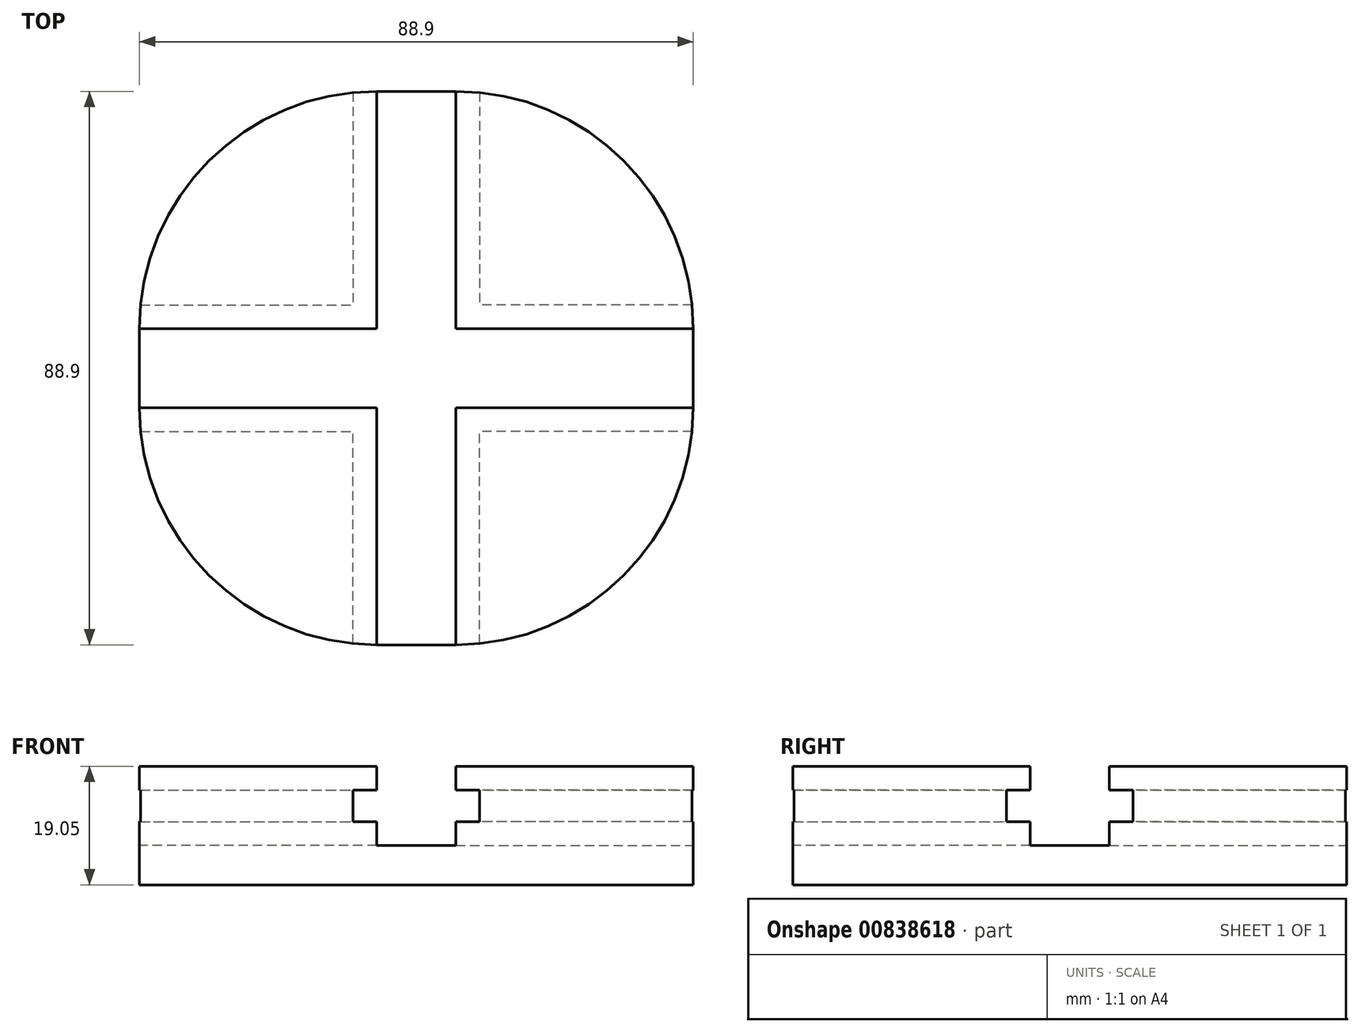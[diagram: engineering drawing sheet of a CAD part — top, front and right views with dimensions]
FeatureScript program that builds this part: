
annotation { "Feature Type Name" : "Feature", "Feature Type Description" : "" }
export const myFeature = defineFeature(function(context is Context, id is Id, definition is map)
    precondition{}
    {
        {
            var Q0;
            Q0=qCreatedBy(makeId("Top.planeOp"),FACE);
            var sketch = newSketch(context, id + "F0", { "sketchPlane" : qUnion([Q0])});
            skLineSegment(sketch, "E0.bottom", {"start": v(0, 0) * mm, "end": v(88.9, 0) * mm});
            skLineSegment(sketch, "E0.top", {"start": v(0, 88.9) * mm, "end": v(88.9, 88.9) * mm});
            skLineSegment(sketch, "E0.left", {"start": v(0, 0) * mm, "end": v(0, 88.9) * mm});
            skLineSegment(sketch, "E0.right", {"start": v(88.9, 0) * mm, "end": v(88.9, 88.9) * mm});
            skSolve(sketch);
        }
        {
            var Q0;
            Q0=makeQuery(id+"F0.imprint","IMPRINT",FACE,{"disambiguationData":[TD([[makeQuery(id+"F0.imprint","IMPRINT",EDGE,{"derivedFrom":sQuery(id+"F0.wireOp",EDGE,"E0.bottom")}),1.0]])]});
            extrude(context, id + "F1", {"entities" : qUnion([Q0]), "depth" : 19.05 * mm, "offsetDistance" : 25.4 * mm});
        }
        {
            var Q0;
            Q0=makeQuery(id+"F1.opExtrude","CAP_FACE",FACE,{"disambiguationData":[OSD([sQuery(id+"F0.wireOp",EDGE,"E0.bottom"),sQuery(id+"F0.wireOp",EDGE,"E0.top"),sQuery(id+"F0.wireOp",EDGE,"E0.left"),sQuery(id+"F0.wireOp",EDGE,"E0.right")])],"isStart":false});
            var sketch = newSketch(context, id + "F2", { "sketchPlane" : qUnion([Q0])});
            skLineSegment(sketch, "E1", {"start": v(0, 50.8) * mm, "end": v(38.1, 50.8) * mm});
            skLineSegment(sketch, "E2", {"start": v(38.1, 50.8) * mm, "end": v(38.1, 88.9) * mm});
            skLineSegment(sketch, "E3", {"start": v(38.1, 88.9) * mm, "end": v(50.8, 88.9) * mm});
            skLineSegment(sketch, "E4", {"start": v(50.8, 88.9) * mm, "end": v(50.8, 50.8) * mm});
            skLineSegment(sketch, "E5", {"start": v(50.8, 50.8) * mm, "end": v(88.9, 50.8) * mm});
            skLineSegment(sketch, "E6", {"start": v(88.9, 50.8) * mm, "end": v(88.9, 38.1) * mm});
            skLineSegment(sketch, "E7", {"start": v(88.9, 38.1) * mm, "end": v(50.8, 38.1) * mm});
            skLineSegment(sketch, "E8", {"start": v(50.8, 38.1) * mm, "end": v(50.8, 0) * mm});
            skLineSegment(sketch, "E9", {"start": v(50.8, 0) * mm, "end": v(38.1, 0) * mm});
            skLineSegment(sketch, "E10", {"start": v(38.1, 0) * mm, "end": v(38.1, 38.1) * mm});
            skLineSegment(sketch, "E11", {"start": v(38.1, 38.1) * mm, "end": v(0, 38.1) * mm});
            skSolve(sketch);
        }
        {
            var Q0;
            {var subQ0=sQuery(id+"F2.wireOp",EDGE,"E1");Q0=makeQuery(id+"F2.imprint","IMPRINT",FACE,{"disambiguationData":[TD([[makeQuery(id+"F2.imprint","IMPRINT",EDGE,{"derivedFrom":subQ0}),-1.0]])]});}
            extrude(context, id + "F3", {"entities" : qUnion([Q0]), "operationType" : NewBodyOperationType.REMOVE, "oppositeDirection" : true, "depth" : 12.7 * mm, "offsetDistance" : 25.4 * mm});
        }
        {
            var Q0;
            Q0=makeQuery(id+"F1.opExtrude","SWEPT_EDGE",EDGE,{"disambiguationData":[OSD([sQuery(id+"F0.wireOp",EDGE,"E0.bottom"),sQuery(id+"F0.wireOp",EDGE,"E0.right")])]});
            var Q1;
            Q1=makeQuery(id+"F1.opExtrude","SWEPT_EDGE",EDGE,{"disambiguationData":[OSD([sQuery(id+"F0.wireOp",EDGE,"E0.bottom"),sQuery(id+"F0.wireOp",EDGE,"E0.left")])]});
            var Q2;
            Q2=makeQuery(id+"F1.opExtrude","SWEPT_EDGE",EDGE,{"disambiguationData":[OSD([sQuery(id+"F0.wireOp",EDGE,"E0.top"),sQuery(id+"F0.wireOp",EDGE,"E0.right")])]});
            var Q3;
            Q3=makeQuery(id+"F1.opExtrude","SWEPT_EDGE",EDGE,{"disambiguationData":[OSD([sQuery(id+"F0.wireOp",EDGE,"E0.top"),sQuery(id+"F0.wireOp",EDGE,"E0.left")])]});
            fillet(context, id + "F4", {"entities" : qUnion([Q0, Q1, Q2, Q3]), "radius" : 38.1 * mm, "tangentPropagation" : true, "allowEdgeOverflow" : false});
        }
        {
            var Q0;
            Q0=makeQuery(id+"F3.boolean.opBoolean","COPY",FACE,{"derivedFrom":makeQuery(id+"F3.opExtrude","SWEPT_FACE",FACE,{"disambiguationData":[OSD([sQuery(id+"F2.wireOp",EDGE,"E7")])]})});
            var sketch = newSketch(context, id + "F5", { "sketchPlane" : qUnion([Q0])});
            skLineSegment(sketch, "E12", {"start": v(-50.8, 15.24) * mm, "end": v(-54.61, 15.24) * mm});
            skLineSegment(sketch, "E13", {"start": v(-54.61, 15.24) * mm, "end": v(-54.61, 10.16) * mm});
            skLineSegment(sketch, "E14", {"start": v(-54.61, 10.16) * mm, "end": v(-50.8, 10.16) * mm});
            skLineSegment(sketch, "E15", {"start": v(-50.8, 10.16) * mm, "end": v(-50.8, 15.24) * mm});
            skSolve(sketch);
        }
        {
            var Q0;
            Q0=makeQuery(id+"F5.imprint","IMPRINT",FACE,{"disambiguationData":[TD([[makeQuery(id+"F5.imprint","IMPRINT",EDGE,{"derivedFrom":sQuery(id+"F5.wireOp",EDGE,"E12")}),1.0]])]});
            extrude(context, id + "F6", {"entities" : qUnion([Q0]), "operationType" : NewBodyOperationType.REMOVE, "oppositeDirection" : true, "depth" : 38.1 * mm, "offsetDistance" : 25.4 * mm});
        }
        {
            var Q0;
            Q0=makeQuery(id+"F3.boolean.opBoolean","COPY",FACE,{"derivedFrom":makeQuery(id+"F3.opExtrude","SWEPT_FACE",FACE,{"disambiguationData":[OSD([sQuery(id+"F2.wireOp",EDGE,"E5")])]})});
            var sketch = newSketch(context, id + "F7", { "sketchPlane" : qUnion([Q0])});
            skLineSegment(sketch, "E16", {"start": v(50.8, 15.24) * mm, "end": v(54.61, 15.24) * mm});
            skLineSegment(sketch, "E17", {"start": v(54.61, 15.24) * mm, "end": v(54.61, 10.16) * mm});
            skLineSegment(sketch, "E18", {"start": v(54.61, 10.16) * mm, "end": v(50.8, 10.16) * mm});
            skLineSegment(sketch, "E19", {"start": v(50.8, 10.16) * mm, "end": v(50.8, 15.24) * mm});
            skSolve(sketch);
        }
        {
            var Q0;
            Q0=makeQuery(id+"F7.imprint","IMPRINT",FACE,{"disambiguationData":[TD([[makeQuery(id+"F7.imprint","IMPRINT",EDGE,{"derivedFrom":sQuery(id+"F7.wireOp",EDGE,"E16")}),-1.0]])]});
            extrude(context, id + "F8", {"entities" : qUnion([Q0]), "operationType" : NewBodyOperationType.REMOVE, "oppositeDirection" : true, "depth" : 38.1 * mm, "offsetDistance" : 25.4 * mm});
        }
        {
            var Q0;
            Q0=makeQuery(id+"F3.boolean.opBoolean","COPY",FACE,{"derivedFrom":makeQuery(id+"F3.opExtrude","SWEPT_FACE",FACE,{"disambiguationData":[OSD([sQuery(id+"F2.wireOp",EDGE,"E10")])]})});
            var sketch = newSketch(context, id + "F9", { "sketchPlane" : qUnion([Q0])});
            skLineSegment(sketch, "E20.bottom", {"start": v(38.1, 15.24) * mm, "end": v(34.3, 15.24) * mm});
            skLineSegment(sketch, "E20.top", {"start": v(38.1, 10.16) * mm, "end": v(34.3, 10.16) * mm});
            skLineSegment(sketch, "E20.left", {"start": v(38.1, 15.24) * mm, "end": v(38.1, 10.16) * mm});
            skLineSegment(sketch, "E20.right", {"start": v(34.3, 15.24) * mm, "end": v(34.3, 10.16) * mm});
            skSolve(sketch);
        }
        {
            var Q0;
            Q0=makeQuery(id+"F9.imprint","IMPRINT",FACE,{"disambiguationData":[TD([[makeQuery(id+"F9.imprint","IMPRINT",EDGE,{"derivedFrom":sQuery(id+"F9.wireOp",EDGE,"E20.bottom")}),1.0]])]});
            extrude(context, id + "F10", {"entities" : qUnion([Q0]), "operationType" : NewBodyOperationType.REMOVE, "oppositeDirection" : true, "depth" : 38.1 * mm, "offsetDistance" : 25.4 * mm});
        }
        {
            var Q0;
            Q0=makeQuery(id+"F6.boolean.opBoolean","COPY",FACE,{"derivedFrom":makeQuery(id+"F6.opExtrude","SWEPT_FACE",FACE,{"disambiguationData":[OSD([sQuery(id+"F5.wireOp",EDGE,"E13")])]})});
            var sketch = newSketch(context, id + "F11", { "sketchPlane" : qUnion([Q0])});
            skLineSegment(sketch, "E21", {"start": v(-38.1, 15.24) * mm, "end": v(-34.3, 15.24) * mm});
            skLineSegment(sketch, "E22", {"start": v(-34.3, 15.24) * mm, "end": v(-34.3, 10.16) * mm});
            skLineSegment(sketch, "E23", {"start": v(-34.3, 10.16) * mm, "end": v(-38.1, 10.16) * mm});
            skLineSegment(sketch, "E24", {"start": v(-38.1, 10.16) * mm, "end": v(-38.1, 15.24) * mm});
            skSolve(sketch);
        }
        {
            var Q0;
            Q0=makeQuery(id+"F11.imprint","IMPRINT",FACE,{"disambiguationData":[TD([[makeQuery(id+"F11.imprint","IMPRINT",EDGE,{"derivedFrom":sQuery(id+"F11.wireOp",EDGE,"E21")}),1.0]])]});
            extrude(context, id + "F12", {"entities" : qUnion([Q0]), "operationType" : NewBodyOperationType.REMOVE, "oppositeDirection" : true, "depth" : 38.1 * mm, "offsetDistance" : 25.4 * mm});
        }
        {
            var Q0;
            Q0=makeQuery(id+"F3.boolean.opBoolean","COPY",FACE,{"derivedFrom":makeQuery(id+"F3.opExtrude","SWEPT_FACE",FACE,{"disambiguationData":[OSD([sQuery(id+"F2.wireOp",EDGE,"E2")])]})});
            var sketch = newSketch(context, id + "F13", { "sketchPlane" : qUnion([Q0])});
            skLineSegment(sketch, "E25.bottom", {"start": v(50.8, 15.24) * mm, "end": v(54.6, 15.24) * mm});
            skLineSegment(sketch, "E25.top", {"start": v(50.8, 10.16) * mm, "end": v(54.6, 10.16) * mm});
            skLineSegment(sketch, "E25.left", {"start": v(50.8, 15.24) * mm, "end": v(50.8, 10.16) * mm});
            skLineSegment(sketch, "E25.right", {"start": v(54.6, 15.24) * mm, "end": v(54.6, 10.16) * mm});
            skSolve(sketch);
        }
        {
            var Q0;
            Q0=makeQuery(id+"F13.imprint","IMPRINT",FACE,{"disambiguationData":[TD([[makeQuery(id+"F13.imprint","IMPRINT",EDGE,{"derivedFrom":sQuery(id+"F13.wireOp",EDGE,"E25.bottom")}),-1.0]])]});
            extrude(context, id + "F14", {"entities" : qUnion([Q0]), "operationType" : NewBodyOperationType.REMOVE, "oppositeDirection" : true, "depth" : 38.1 * mm, "offsetDistance" : 25.4 * mm});
        }
        {
            var Q0;
            Q0=makeQuery(id+"F8.boolean.opBoolean","COPY",FACE,{"derivedFrom":makeQuery(id+"F8.opExtrude","SWEPT_FACE",FACE,{"disambiguationData":[OSD([sQuery(id+"F7.wireOp",EDGE,"E17")])]})});
            var sketch = newSketch(context, id + "F15", { "sketchPlane" : qUnion([Q0])});
            skLineSegment(sketch, "E26.bottom", {"start": v(-50.8, 15.24) * mm, "end": v(-54.6, 15.24) * mm});
            skLineSegment(sketch, "E26.top", {"start": v(-50.8, 10.16) * mm, "end": v(-54.6, 10.16) * mm});
            skLineSegment(sketch, "E26.left", {"start": v(-50.8, 15.24) * mm, "end": v(-50.8, 10.16) * mm});
            skLineSegment(sketch, "E26.right", {"start": v(-54.6, 15.24) * mm, "end": v(-54.6, 10.16) * mm});
            skSolve(sketch);
        }
        {
            var Q0;
            Q0=makeQuery(id+"F15.imprint","IMPRINT",FACE,{"disambiguationData":[TD([[makeQuery(id+"F15.imprint","IMPRINT",EDGE,{"derivedFrom":sQuery(id+"F15.wireOp",EDGE,"E26.bottom")}),-1.0]])]});
            extrude(context, id + "F16", {"entities" : qUnion([Q0]), "operationType" : NewBodyOperationType.REMOVE, "oppositeDirection" : true, "depth" : 38.1 * mm, "offsetDistance" : 25.4 * mm});
        }
        {
            var Q0;
            Q0=makeQuery(id+"F14.boolean.opBoolean","COPY",FACE,{"derivedFrom":makeQuery(id+"F14.opExtrude","SWEPT_FACE",FACE,{"disambiguationData":[OSD([sQuery(id+"F13.wireOp",EDGE,"E25.right")])]})});
            var sketch = newSketch(context, id + "F17", { "sketchPlane" : qUnion([Q0])});
            skLineSegment(sketch, "E27.bottom", {"start": v(38.1, 15.24) * mm, "end": v(34.29, 15.24) * mm});
            skLineSegment(sketch, "E27.top", {"start": v(38.1, 10.16) * mm, "end": v(34.29, 10.16) * mm});
            skLineSegment(sketch, "E27.left", {"start": v(38.1, 15.24) * mm, "end": v(38.1, 10.16) * mm});
            skLineSegment(sketch, "E27.right", {"start": v(34.29, 15.24) * mm, "end": v(34.29, 10.16) * mm});
            skSolve(sketch);
        }
        {
            var Q0;
            Q0=makeQuery(id+"F17.imprint","IMPRINT",FACE,{"disambiguationData":[TD([[makeQuery(id+"F17.imprint","IMPRINT",EDGE,{"derivedFrom":sQuery(id+"F17.wireOp",EDGE,"E27.bottom")}),-1.0]])]});
            extrude(context, id + "F18", {"entities" : qUnion([Q0]), "operationType" : NewBodyOperationType.REMOVE, "oppositeDirection" : true, "depth" : 38.1 * mm, "offsetDistance" : 25.4 * mm});
        }
        {
            var Q0;
            Q0=makeQuery(id+"F10.boolean.opBoolean","COPY",FACE,{"derivedFrom":makeQuery(id+"F10.opExtrude","SWEPT_FACE",FACE,{"disambiguationData":[OSD([sQuery(id+"F9.wireOp",EDGE,"E20.right")])]})});
            var sketch = newSketch(context, id + "F19", { "sketchPlane" : qUnion([Q0])});
            skLineSegment(sketch, "E28.bottom", {"start": v(-38.1, 15.24) * mm, "end": v(-34.29, 15.24) * mm});
            skLineSegment(sketch, "E28.top", {"start": v(-38.1, 10.16) * mm, "end": v(-34.29, 10.16) * mm});
            skLineSegment(sketch, "E28.left", {"start": v(-38.1, 15.24) * mm, "end": v(-38.1, 10.16) * mm});
            skLineSegment(sketch, "E28.right", {"start": v(-34.29, 15.24) * mm, "end": v(-34.29, 10.16) * mm});
            skSolve(sketch);
        }
        {
            var Q0;
            Q0=makeQuery(id+"F19.imprint","IMPRINT",FACE,{"disambiguationData":[TD([[makeQuery(id+"F19.imprint","IMPRINT",EDGE,{"derivedFrom":sQuery(id+"F19.wireOp",EDGE,"E28.bottom")}),1.0]])]});
            extrude(context, id + "F20", {"entities" : qUnion([Q0]), "operationType" : NewBodyOperationType.REMOVE, "oppositeDirection" : true, "depth" : 38.1 * mm, "offsetDistance" : 25.4 * mm});
        }
    });
